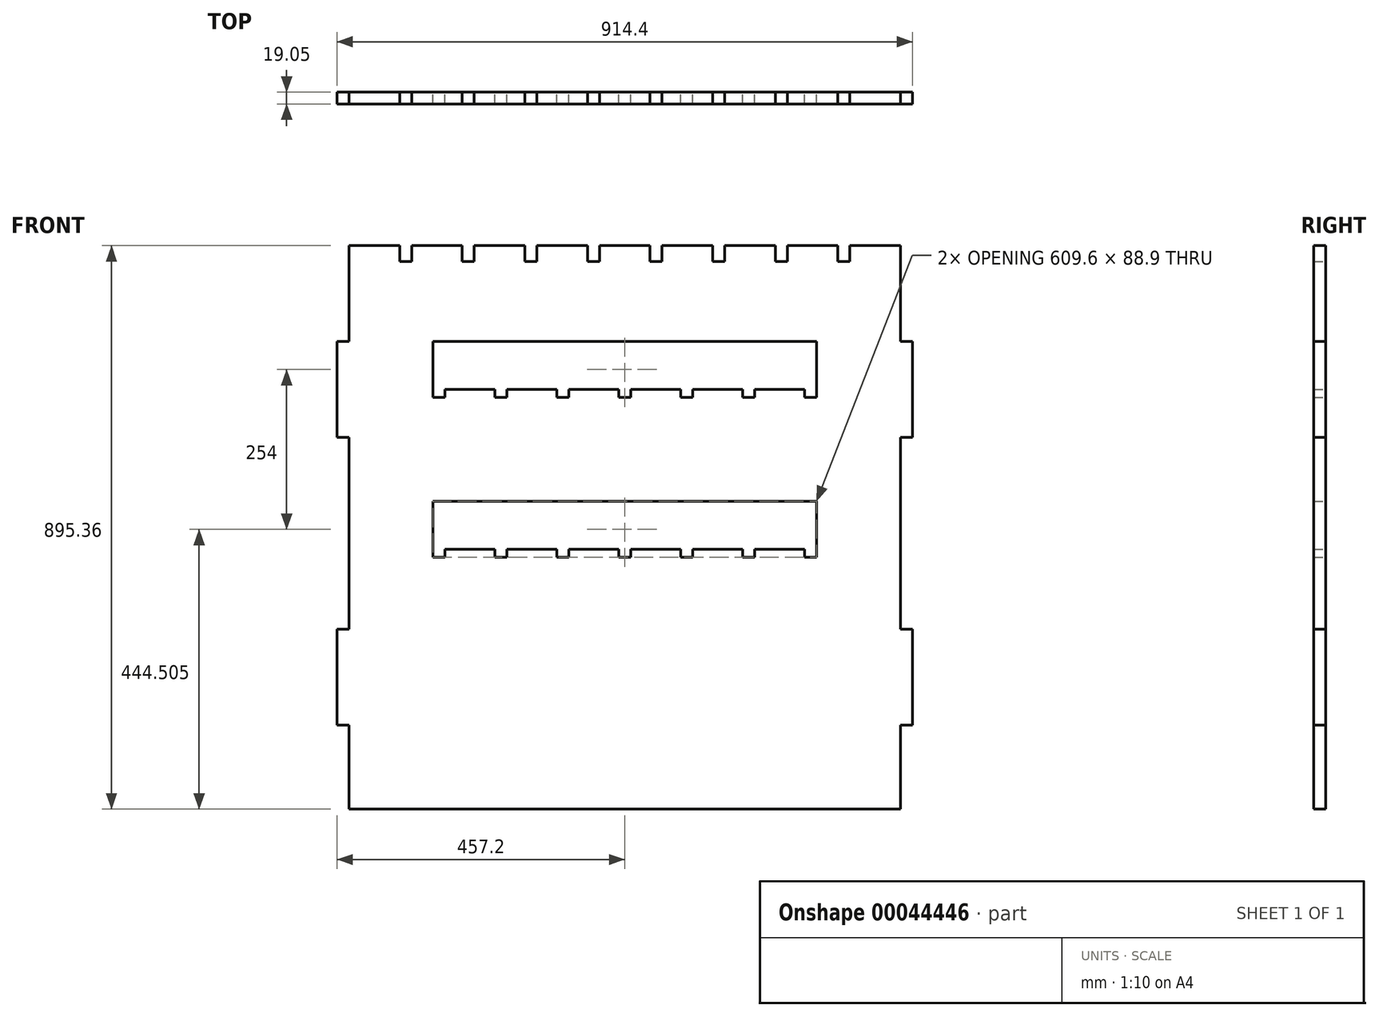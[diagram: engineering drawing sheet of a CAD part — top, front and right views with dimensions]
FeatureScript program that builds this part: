
annotation { "Feature Type Name" : "Feature", "Feature Type Description" : "" }
export const myFeature = defineFeature(function(context is Context, id is Id, definition is map)
    precondition{}
    {
        {
            var Q0;
            Q0=qCreatedBy(makeId("Front.planeOp"),FACE);
            var sketch = newSketch(context, id + "F0", { "sketchPlane" : qUnion([Q0])});
            skLineSegment(sketch, "E0.rect.bottom", {"start": v(-438.15, -447.68) * mm, "end": v(438.15, -447.68) * mm});
            skLineSegment(sketch, "E0.rect.top", {"start": v(-438.15, 447.68) * mm, "end": v(438.15, 447.68) * mm});
            skLineSegment(sketch, "E0.rect.left", {"start": v(-438.15, -447.68) * mm, "end": v(-438.15, 447.68) * mm});
            skLineSegment(sketch, "E0.rect.right", {"start": v(438.15, -447.68) * mm, "end": v(438.15, 447.68) * mm});
            skPoint(sketch, "E0.rect.middle", {"position": v(0, 0) * mm});
            skLineSegment(sketch, "E1.bottom", {"start": v(-438.15, 295.28) * mm, "end": v(-457.2, 295.28) * mm});
            skLineSegment(sketch, "E1.top", {"start": v(-438.15, 142.87) * mm, "end": v(-457.2, 142.87) * mm});
            skLineSegment(sketch, "E1.left", {"start": v(-438.15, 295.28) * mm, "end": v(-438.15, 142.87) * mm});
            skLineSegment(sketch, "E1.right", {"start": v(-457.2, 295.28) * mm, "end": v(-457.2, 142.87) * mm});
            skLineSegment(sketch, "E2.bottom", {"start": v(-438.15, -161.92) * mm, "end": v(-457.2, -161.92) * mm});
            skLineSegment(sketch, "E2.top", {"start": v(-438.15, -314.32) * mm, "end": v(-457.2, -314.32) * mm});
            skLineSegment(sketch, "E2.left", {"start": v(-438.15, -161.92) * mm, "end": v(-438.15, -314.32) * mm});
            skLineSegment(sketch, "E2.right", {"start": v(-457.2, -161.92) * mm, "end": v(-457.2, -314.32) * mm});
            skLineSegment(sketch, "E3.MirrorCS", {"start": v(438.15, -314.32) * mm, "end": v(457.2, -314.32) * mm});
            skLineSegment(sketch, "E4.MirrorCS", {"start": v(438.15, 142.88) * mm, "end": v(457.2, 142.88) * mm});
            skLineSegment(sketch, "E5.MirrorCS", {"start": v(438.15, -161.92) * mm, "end": v(457.2, -161.92) * mm});
            skLineSegment(sketch, "E6.MirrorCS", {"start": v(438.15, 295.28) * mm, "end": v(457.2, 295.28) * mm});
            skLineSegment(sketch, "E7.MirrorCS", {"start": v(457.2, -161.92) * mm, "end": v(457.2, -314.32) * mm});
            skLineSegment(sketch, "E8.MirrorCS", {"start": v(438.15, -161.92) * mm, "end": v(438.15, -314.32) * mm});
            skLineSegment(sketch, "E9.MirrorCS", {"start": v(438.15, 295.28) * mm, "end": v(438.15, 142.87) * mm});
            skLineSegment(sketch, "E10.bottom", {"start": v(-304.8, -34.92) * mm, "end": v(304.8, -34.92) * mm});
            skLineSegment(sketch, "E10.top", {"start": v(-304.8, 41.28) * mm, "end": v(304.8, 41.28) * mm});
            skLineSegment(sketch, "E10.left", {"start": v(-304.8, -34.92) * mm, "end": v(-304.8, 41.28) * mm});
            skLineSegment(sketch, "E10.right", {"start": v(304.8, -34.92) * mm, "end": v(304.8, 41.28) * mm});
            skLineSegment(sketch, "E11.top", {"start": v(304.8, 295.28) * mm, "end": v(-304.8, 295.27) * mm});
            skLineSegment(sketch, "E11.left", {"start": v(304.8, 219.08) * mm, "end": v(304.8, 295.27) * mm});
            skLineSegment(sketch, "E11.right", {"start": v(-304.8, 219.07) * mm, "end": v(-304.8, 295.27) * mm});
            skLineSegment(sketch, "E12.bottom", {"start": v(-206.38, 219.07) * mm, "end": v(-187.33, 219.07) * mm});
            skLineSegment(sketch, "E12.top", {"start": v(-206.38, 206.37) * mm, "end": v(-187.33, 206.37) * mm});
            skLineSegment(sketch, "E12.left", {"start": v(-206.38, 219.08) * mm, "end": v(-206.38, 206.38) * mm});
            skLineSegment(sketch, "E12.right", {"start": v(-187.33, 219.08) * mm, "end": v(-187.33, 206.38) * mm});
            skLineSegment(sketch, "E13.bottom", {"start": v(-107.95, 219.07) * mm, "end": v(-88.9, 219.07) * mm});
            skLineSegment(sketch, "E13.top", {"start": v(-107.95, 206.37) * mm, "end": v(-88.9, 206.37) * mm});
            skLineSegment(sketch, "E13.left", {"start": v(-107.95, 219.08) * mm, "end": v(-107.95, 206.38) * mm});
            skLineSegment(sketch, "E13.right", {"start": v(-88.9, 219.08) * mm, "end": v(-88.9, 206.38) * mm});
            skLineSegment(sketch, "E14.bottom", {"start": v(-9.53, 219.07) * mm, "end": v(9.53, 219.07) * mm});
            skLineSegment(sketch, "E14.top", {"start": v(-9.53, 206.38) * mm, "end": v(9.53, 206.38) * mm});
            skLineSegment(sketch, "E14.left", {"start": v(-9.53, 219.08) * mm, "end": v(-9.53, 206.38) * mm});
            skLineSegment(sketch, "E14.right", {"start": v(9.52, 219.08) * mm, "end": v(9.52, 206.38) * mm});
            skLineSegment(sketch, "E15.bottom", {"start": v(88.9, 219.08) * mm, "end": v(107.95, 219.08) * mm});
            skLineSegment(sketch, "E15.top", {"start": v(88.9, 206.38) * mm, "end": v(107.95, 206.38) * mm});
            skLineSegment(sketch, "E15.left", {"start": v(88.9, 219.08) * mm, "end": v(88.9, 206.38) * mm});
            skLineSegment(sketch, "E15.right", {"start": v(107.95, 219.08) * mm, "end": v(107.95, 206.38) * mm});
            skLineSegment(sketch, "E16.bottom", {"start": v(187.33, 219.08) * mm, "end": v(206.38, 219.08) * mm});
            skLineSegment(sketch, "E16.top", {"start": v(187.33, 206.38) * mm, "end": v(206.38, 206.38) * mm});
            skLineSegment(sketch, "E16.left", {"start": v(187.32, 219.08) * mm, "end": v(187.32, 206.38) * mm});
            skLineSegment(sketch, "E16.right", {"start": v(206.38, 219.08) * mm, "end": v(206.38, 206.38) * mm});
            skLineSegment(sketch, "E17.right", {"start": v(-187.32, -34.93) * mm, "end": v(-187.32, -47.63) * mm});
            skLineSegment(sketch, "E17.left", {"start": v(-206.38, -34.93) * mm, "end": v(-206.38, -47.63) * mm});
            skLineSegment(sketch, "E17.bottom", {"start": v(-206.37, -34.92) * mm, "end": v(-187.32, -34.92) * mm});
            skLineSegment(sketch, "E17.top", {"start": v(-206.38, -47.62) * mm, "end": v(-187.32, -47.62) * mm});
            skLineSegment(sketch, "E18.bottom", {"start": v(-107.95, -34.92) * mm, "end": v(-88.9, -34.92) * mm});
            skLineSegment(sketch, "E18.top", {"start": v(-107.95, -47.62) * mm, "end": v(-88.9, -47.62) * mm});
            skLineSegment(sketch, "E18.left", {"start": v(-107.95, -34.93) * mm, "end": v(-107.95, -47.63) * mm});
            skLineSegment(sketch, "E18.right", {"start": v(-88.9, -34.93) * mm, "end": v(-88.9, -47.63) * mm});
            skLineSegment(sketch, "E19.bottom", {"start": v(-9.53, -34.92) * mm, "end": v(9.53, -34.92) * mm});
            skLineSegment(sketch, "E19.top", {"start": v(-9.52, -47.62) * mm, "end": v(9.53, -47.62) * mm});
            skLineSegment(sketch, "E19.left", {"start": v(-9.52, -34.92) * mm, "end": v(-9.52, -47.63) * mm});
            skLineSegment(sketch, "E19.right", {"start": v(9.53, -34.93) * mm, "end": v(9.53, -47.63) * mm});
            skLineSegment(sketch, "E20.bottom", {"start": v(187.32, -34.92) * mm, "end": v(206.37, -34.92) * mm});
            skLineSegment(sketch, "E20.top", {"start": v(187.33, -47.62) * mm, "end": v(206.38, -47.62) * mm});
            skLineSegment(sketch, "E20.left", {"start": v(187.33, -34.92) * mm, "end": v(187.33, -47.63) * mm});
            skLineSegment(sketch, "E20.right", {"start": v(206.38, -34.92) * mm, "end": v(206.38, -47.63) * mm});
            skLineSegment(sketch, "E21.bottom", {"start": v(88.9, -34.92) * mm, "end": v(107.95, -34.92) * mm});
            skLineSegment(sketch, "E21.top", {"start": v(88.9, -47.62) * mm, "end": v(107.95, -47.62) * mm});
            skLineSegment(sketch, "E21.left", {"start": v(88.9, -34.92) * mm, "end": v(88.9, -47.63) * mm});
            skLineSegment(sketch, "E21.right", {"start": v(107.95, -34.93) * mm, "end": v(107.95, -47.63) * mm});
            skLineSegment(sketch, "E22", {"start": v(-304.8, 219.07) * mm, "end": v(304.8, 219.08) * mm});
            skLineSegment(sketch, "E23.bottom", {"start": v(-357.72, 447.68) * mm, "end": v(-338.67, 447.68) * mm});
            skLineSegment(sketch, "E23.top", {"start": v(-357.72, 422.28) * mm, "end": v(-338.67, 422.28) * mm});
            skLineSegment(sketch, "E23.left", {"start": v(-357.72, 447.68) * mm, "end": v(-357.72, 422.28) * mm});
            skLineSegment(sketch, "E23.right", {"start": v(-338.67, 447.68) * mm, "end": v(-338.67, 422.28) * mm});
            skLineSegment(sketch, "E24.bottom", {"start": v(-258.23, 447.68) * mm, "end": v(-239.18, 447.68) * mm});
            skLineSegment(sketch, "E24.top", {"start": v(-258.23, 422.28) * mm, "end": v(-239.18, 422.28) * mm});
            skLineSegment(sketch, "E24.left", {"start": v(-258.23, 447.68) * mm, "end": v(-258.23, 422.28) * mm});
            skLineSegment(sketch, "E24.right", {"start": v(-239.18, 447.68) * mm, "end": v(-239.18, 422.28) * mm});
            skLineSegment(sketch, "E25.bottom", {"start": v(-158.75, 447.68) * mm, "end": v(-139.7, 447.68) * mm});
            skLineSegment(sketch, "E25.top", {"start": v(-158.75, 422.28) * mm, "end": v(-139.7, 422.28) * mm});
            skLineSegment(sketch, "E25.left", {"start": v(-158.75, 447.68) * mm, "end": v(-158.75, 422.28) * mm});
            skLineSegment(sketch, "E25.right", {"start": v(-139.7, 447.68) * mm, "end": v(-139.7, 422.28) * mm});
            skLineSegment(sketch, "E26.bottom", {"start": v(-59.27, 447.68) * mm, "end": v(-40.22, 447.68) * mm});
            skLineSegment(sketch, "E26.top", {"start": v(-59.27, 422.28) * mm, "end": v(-40.22, 422.28) * mm});
            skLineSegment(sketch, "E26.left", {"start": v(-59.27, 447.68) * mm, "end": v(-59.27, 422.28) * mm});
            skLineSegment(sketch, "E26.right", {"start": v(-40.22, 447.68) * mm, "end": v(-40.22, 422.28) * mm});
            skLineSegment(sketch, "E27.MirrorCS", {"start": v(158.75, 422.28) * mm, "end": v(139.7, 422.28) * mm});
            skLineSegment(sketch, "E28.MirrorCS", {"start": v(59.27, 447.68) * mm, "end": v(40.22, 447.68) * mm});
            skLineSegment(sketch, "E29.MirrorCS", {"start": v(158.75, 447.68) * mm, "end": v(139.7, 447.68) * mm});
            skLineSegment(sketch, "E30.MirrorCS", {"start": v(357.72, 422.28) * mm, "end": v(338.67, 422.28) * mm});
            skLineSegment(sketch, "E31.MirrorCS", {"start": v(357.72, 447.68) * mm, "end": v(338.67, 447.68) * mm});
            skLineSegment(sketch, "E32.MirrorCS", {"start": v(59.27, 422.28) * mm, "end": v(40.22, 422.28) * mm});
            skLineSegment(sketch, "E33.MirrorCS", {"start": v(258.23, 447.68) * mm, "end": v(239.18, 447.68) * mm});
            skLineSegment(sketch, "E34.MirrorCS", {"start": v(258.23, 422.28) * mm, "end": v(239.18, 422.28) * mm});
            skLineSegment(sketch, "E35.MirrorCS", {"start": v(338.67, 447.68) * mm, "end": v(338.67, 422.28) * mm});
            skLineSegment(sketch, "E36.MirrorCS", {"start": v(158.75, 447.68) * mm, "end": v(158.75, 422.28) * mm});
            skLineSegment(sketch, "E37.MirrorCS", {"start": v(438.15, 447.68) * mm, "end": v(-438.15, 447.68) * mm});
            skLineSegment(sketch, "E38.MirrorCS", {"start": v(357.72, 447.68) * mm, "end": v(357.72, 422.28) * mm});
            skLineSegment(sketch, "E39.MirrorCS", {"start": v(40.22, 447.68) * mm, "end": v(40.22, 422.28) * mm});
            skLineSegment(sketch, "E40.MirrorCS", {"start": v(239.18, 447.68) * mm, "end": v(239.18, 422.28) * mm});
            skLineSegment(sketch, "E41.MirrorCS", {"start": v(59.27, 447.68) * mm, "end": v(59.27, 422.28) * mm});
            skLineSegment(sketch, "E42.MirrorCS", {"start": v(139.7, 447.68) * mm, "end": v(139.7, 422.28) * mm});
            skLineSegment(sketch, "E43.MirrorCS", {"start": v(258.23, 447.68) * mm, "end": v(258.23, 422.28) * mm});
            skLineSegment(sketch, "E44.bottom", {"start": v(-152.4, -447.68) * mm, "end": v(152.4, -447.68) * mm});
            skLineSegment(sketch, "E44.top", {"start": v(-152.4, -485.78) * mm, "end": v(152.4, -485.78) * mm});
            skLineSegment(sketch, "E44.left", {"start": v(-152.4, -447.68) * mm, "end": v(-152.4, -485.78) * mm});
            skLineSegment(sketch, "E44.right", {"start": v(152.4, -447.68) * mm, "end": v(152.4, -485.78) * mm});
            skLineSegment(sketch, "E45", {"start": v(457.2, 295.28) * mm, "end": v(457.2, 142.87) * mm});
            skLineSegment(sketch, "E46.bottom", {"start": v(304.8, 219.08) * mm, "end": v(285.75, 219.08) * mm});
            skLineSegment(sketch, "E46.top", {"start": v(304.8, 206.38) * mm, "end": v(285.75, 206.38) * mm});
            skLineSegment(sketch, "E46.left", {"start": v(304.8, 219.08) * mm, "end": v(304.8, 206.38) * mm});
            skLineSegment(sketch, "E46.right", {"start": v(285.75, 219.08) * mm, "end": v(285.75, 206.38) * mm});
            skLineSegment(sketch, "E47.bottom", {"start": v(-304.8, 219.07) * mm, "end": v(-285.75, 219.07) * mm});
            skLineSegment(sketch, "E47.top", {"start": v(-304.8, 206.38) * mm, "end": v(-285.75, 206.38) * mm});
            skLineSegment(sketch, "E47.left", {"start": v(-304.8, 219.07) * mm, "end": v(-304.8, 206.38) * mm});
            skLineSegment(sketch, "E47.right", {"start": v(-285.75, 219.07) * mm, "end": v(-285.75, 206.38) * mm});
            skLineSegment(sketch, "E48.bottom", {"start": v(-304.8, -34.92) * mm, "end": v(-285.75, -34.92) * mm});
            skLineSegment(sketch, "E48.top", {"start": v(-304.8, -47.62) * mm, "end": v(-285.75, -47.62) * mm});
            skLineSegment(sketch, "E48.left", {"start": v(-304.8, -34.92) * mm, "end": v(-304.8, -47.62) * mm});
            skLineSegment(sketch, "E48.right", {"start": v(-285.75, -34.92) * mm, "end": v(-285.75, -47.62) * mm});
            skLineSegment(sketch, "E49.bottom", {"start": v(304.8, -34.92) * mm, "end": v(285.75, -34.92) * mm});
            skLineSegment(sketch, "E49.top", {"start": v(304.8, -47.62) * mm, "end": v(285.75, -47.62) * mm});
            skLineSegment(sketch, "E49.left", {"start": v(304.8, -34.92) * mm, "end": v(304.8, -47.62) * mm});
            skLineSegment(sketch, "E49.right", {"start": v(285.75, -34.92) * mm, "end": v(285.75, -47.62) * mm});
            skSolve(sketch);
        }
        {
            var Q0;
            {var subQ2=sQuery(id+"F0.wireOp",EDGE,"E0.rect.top");Q0=makeQuery(id+"F0.imprint","IMPRINT",FACE,{"disambiguationData":[TD([[makeQuery(id+"F0.imprint","IMPRINT",EDGE,{"derivedFrom":subQ2}),-1.0]])]});}
            var Q1;
            Q1=makeQuery(id+"F0.imprint","IMPRINT",FACE,{"disambiguationData":[TD([[makeQuery(id+"F0.imprint","IMPRINT",EDGE,{"derivedFrom":sQuery(id+"F0.wireOp",EDGE,"E1.bottom")}),1.0]])]});
            var Q2;
            Q2=makeQuery(id+"F0.imprint","IMPRINT",FACE,{"disambiguationData":[TD([[makeQuery(id+"F0.imprint","IMPRINT",EDGE,{"derivedFrom":sQuery(id+"F0.wireOp",EDGE,"E2.bottom")}),1.0]])]});
            var Q3;
            Q3=makeQuery(id+"F0.imprint","IMPRINT",FACE,{"disambiguationData":[TD([[makeQuery(id+"F0.imprint","IMPRINT",EDGE,{"derivedFrom":sQuery(id+"F0.wireOp",EDGE,"cb949e54-7a22-4356-aaf1-f9dbaef3b247.bottom")}),-1.0]])]});
            var Q4;
            Q4=makeQuery(id+"F0.imprint","IMPRINT",FACE,{"disambiguationData":[TD([[makeQuery(id+"F0.imprint","IMPRINT",EDGE,{"derivedFrom":sQuery(id+"F0.wireOp",EDGE,"01c8e75c-1472-4d96-a38b-7d7c5dca95fb4.MirrorCS")}),1.0]])]});
            var Q5;
            Q5=makeQuery(id+"F0.imprint","IMPRINT",FACE,{"disambiguationData":[TD([[makeQuery(id+"F0.imprint","IMPRINT",EDGE,{"derivedFrom":sQuery(id+"F0.wireOp",EDGE,"E4.MirrorCS")}),1.0]])]});
            var Q6;
            {var subQ2=sQuery(id+"F0.wireOp",EDGE,"E3.MirrorCS");Q6=makeQuery(id+"F0.imprint","IMPRINT",FACE,{"disambiguationData":[TD([[makeQuery(id+"F0.imprint","IMPRINT",EDGE,{"derivedFrom":subQ2}),1.0]])]});}
            var Q7;
            {var subQ19=sQuery(id+"F0.wireOp",EDGE,"E1.left");Q7=makeQuery(id+"F0.imprint","IMPRINT",FACE,{"disambiguationData":[TD([[makeQuery(id+"F0.imprint","IMPRINT",EDGE,{"derivedFrom":subQ19}),1.0]])]});}
            var Q8;
            Q8=makeQuery(id+"F0.imprint","IMPRINT",FACE,{"disambiguationData":[TD([[makeQuery(id+"F0.imprint","IMPRINT",EDGE,{"derivedFrom":sQuery(id+"F0.wireOp",EDGE,"E44.bottom")}),-1.0]])]});
            extrude(context, id + "F1", {"entities" : qUnion([Q0, Q1, Q2, Q3, Q4, Q5, Q6, Q7, Q8]), "depth" : 19.05 * mm});
        }
    });
